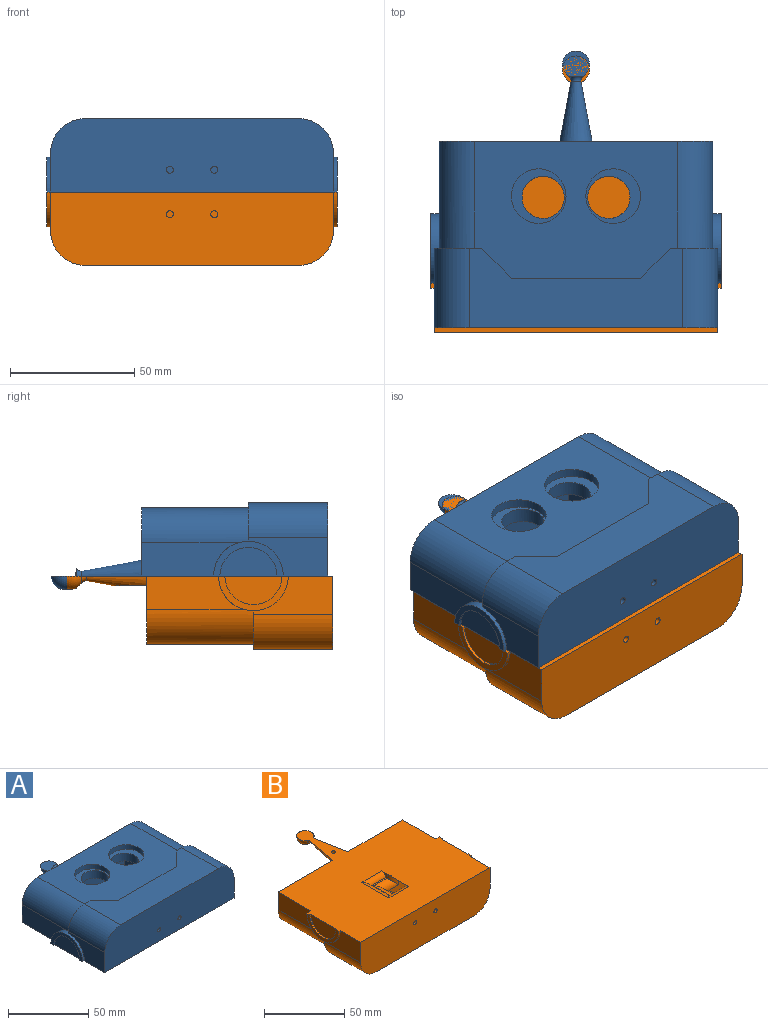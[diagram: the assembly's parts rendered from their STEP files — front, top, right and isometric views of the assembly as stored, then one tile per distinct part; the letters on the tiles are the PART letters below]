
ASSEMBLY  parts=2 mates=1
PART A: 52 faces, bbox 117x111.5x35 mm
  f0: cylinder r=8.5mm len=17mm, axis (0,0,1), area 320.4mm2, adj f1,f51
  f1: plane 22x22mm, normal (0,0,1), area 153.2mm2, adj f0,f2
  f2: cylinder r=11mm len=22mm, axis (0,0,1), area 241.9mm2, adj f1,f3
  f3: plane 82x55.04mm, normal (0,0,1), area 3536.4mm2, adj f2,f4,f41,f42,f43,f44,f45,f46
  f4: plane 12.04x12mm, normal (-0.71,0.71,0), area 34mm2, adj f3,f5,f41,f47
  f5: plane 86x32mm, normal (0,0,1), area 1981.3mm2, adj f4,f6,f35,f40,f41,f42,f43,f47
  f6: cylinder r=14mm len=32mm, axis (0,-1,0), area 703.7mm2, adj f5,f7,f35,f47
  f7: plane 32x15.5mm, normal (1,0,0), area 342.1mm2, adj f6,f8,f13,f35,f47
  f8: cylinder r=14mm len=28mm, axis (-1,0,0), area 109.9mm2, adj f7,f9,f10,f13,f46,f47
  f9: plane 39.31x13.52mm, normal (1,0,0), area 427.8mm2, adj f8,f13,f45,f46
  f10: plane 28x14mm, normal (1,0,0), area 100.1mm2, adj f8,f11,f13
  f11: cylinder r=11.5mm len=23mm, axis (-1,0,0), area 36.1mm2, adj f10,f12,f13
  f12: plane 23x11.5mm, normal (1,0,0), area 207.7mm2, adj f11,f13
  f13: plane 117x111.46mm, normal (0,0,-1), area 7484.9mm2, adj f7,f8,f9,f10,f11,f12,f14,f15
  f14: sphere r=5.5mm, area 175.7mm2, adj f13,f15
  f15: torus R=3.97mm, axis (0,-1,0), area 16.9mm2, adj f13,f14,f16
  f16: cone r=2mm half-angle=10.5deg, axis (0,-1,0), area 329.1mm2, adj f13,f15,f45
  f17: plane 39.31x13.52mm, normal (-1,0,0), area 427.8mm2, adj f13,f21,f44,f45
  f18: plane 23x11.5mm, normal (-1,0,0), area 207.7mm2, adj f13,f19
  f19: cylinder r=11.5mm len=23mm, axis (1,0,0), area 36.1mm2, adj f13,f18,f20
  f20: plane 28x14mm, normal (-1,0,0), area 100.1mm2, adj f13,f19,f21
  f21: cylinder r=14mm len=28mm, axis (1,0,0), area 110.1mm2, adj f13,f17,f20,f22,f43,f44
  f22: plane 32x15.5mm, normal (-1,0,0), area 342.1mm2, adj f13,f21,f35,f40,f43
  f23: plane 22x18mm, normal (1,0,0), area 396mm2, adj f13,f24,f32,f51
  f24: plane 47x18mm, normal (0,-1,0), area 846mm2, adj f13,f23,f25,f51
  f25: plane 22x18mm, normal (-1,0,0), area 396mm2, adj f13,f24,f32,f51
  f26: cylinder r=5mm len=17mm, axis (0,0,1), area 133.5mm2, adj f13,f27,f28,f32
  f27: plane 23.5x18mm, normal (0,0,-1), area 253.7mm2, adj f26,f28,f29,f30,f31,f32
  f28: plane 17x13mm, normal (-1,0,0), area 221mm2, adj f13,f26,f27,f29
  f29: plane 17x13.5mm, normal (0,1,0), area 229.5mm2, adj f13,f27,f28,f30
  f30: plane 17x13mm, normal (1,0,0), area 221mm2, adj f13,f27,f29,f31
  f31: cylinder r=5mm len=17mm, axis (0,0,1), area 133.5mm2, adj f13,f27,f30,f32
  f32: plane 47x18mm, normal (0,1,0), area 446.5mm2, adj f13,f23,f25,f26,f27,f31,f51
  f33: cylinder r=1.4mm len=4mm, axis (0,0,-1), area 35.2mm2, adj f13,f34
  f34: plane 2.8x2.8mm, normal (0,0,-1), area 6.2mm2, adj f33
  f35: plane 114x29.5mm, normal (0,-1,0), area 3266.6mm2, adj f5,f6,f7,f13,f22,f36,f38,f40
  f36: cylinder r=1.4mm len=10mm, axis (0,-1,0), area 88mm2, adj f35,f37
  f37: plane 2.8x2.8mm, normal (0,-1,0), area 6.2mm2, adj f36
  f38: cylinder r=1.4mm len=10mm, axis (0,-1,0), area 88mm2, adj f35,f39
  f39: plane 2.8x2.8mm, normal (0,-1,0), area 6.2mm2, adj f38
  f40: cylinder r=14mm len=32mm, axis (0,-1,0), area 703.7mm2, adj f5,f22,f35,f43
  f41: plane 52x2mm, normal (0,1,0), area 104mm2, adj f3,f4,f5,f42
  f42: plane 12.04x12mm, normal (0.71,0.71,0), area 34mm2, adj f3,f5,f41,f43
  f43: plane 19.02x15.62mm, normal (0,1,0), area 65mm2, adj f3,f5,f21,f22,f40,f42,f44
  f44: cylinder r=14mm len=43mm, axis (0,1,0), area 944.7mm2, adj f3,f17,f21,f43,f45
  f45: plane 110x27.5mm, normal (0,1,0), area 2874.5mm2, adj f3,f9,f13,f16,f17,f44,f46
  f46: cylinder r=14mm len=43mm, axis (0,-1,0), area 944.7mm2, adj f3,f8,f9,f45,f47
  f47: plane 19.02x15.62mm, normal (0,1,0), area 65mm2, adj f3,f4,f5,f6,f7,f8,f46
  f48: cylinder r=11mm len=22mm, axis (0,0,1), area 241.9mm2, adj f3,f49
  f49: plane 22x22mm, normal (0,0,1), area 153.2mm2, adj f48,f50
  f50: cylinder r=8.5mm len=17mm, axis (0,0,1), area 320.4mm2, adj f49,f51
  f51: plane 47x22mm, normal (0,0,-1), area 580mm2, adj f0,f23,f24,f25,f32,f50
PART B: 66 faces, bbox 117.4x111.9x29.9 mm
  f0: plane 18.53x15.62mm, normal (0,1,0), area 63.9mm2, adj f1,f2,f11,f14,f15,f24,f50
  f1: plane 86x32mm, normal (0,0,-1), area 992.9mm2, adj f0,f3,f5,f6,f13,f14,f33,f34
  f2: plane 82x43mm, normal (0,0,-1), area 1071.7mm2, adj f0,f6,f10,f15,f16,f32,f34,f35
  f3: plane 16x16mm, normal (-1,0,0), area 256mm2, adj f1,f33,f38,f60
  f4: plane 16.13x13.5mm, normal (0,0,1), area 37.7mm2, adj f47,f56,f57,f63,f64,f65
  f5: plane 114x29.5mm, normal (0,-1,0), area 3266.6mm2, adj f1,f11,f12,f13,f14,f20,f22,f31
  f6: plane 26.02x15.62mm, normal (0,1,0), area 78.9mm2, adj f1,f2,f12,f13,f16,f28,f34
  f7: plane 39.31x13.52mm, normal (-1,0,0), area 427.8mm2, adj f10,f16,f28,f31
  f8: cylinder r=11.5mm len=23mm, axis (-1,0,0), area 36.1mm2, adj f25,f26,f31
  f9: plane 39.31x13.52mm, normal (1,0,0), area 427.8mm2, adj f10,f15,f24,f31
  f10: plane 110x27.5mm, normal (0,1,0), area 2892.4mm2, adj f2,f7,f9,f15,f16,f18,f31,f54
  f11: plane 32x15.5mm, normal (1,0,0), area 342.1mm2, adj f0,f5,f14,f24,f31
  f12: plane 32x15.5mm, normal (-1,0,0), area 342.1mm2, adj f5,f6,f13,f28,f31
  f13: cylinder r=14mm len=32mm, axis (0,-1,0), area 703.7mm2, adj f1,f5,f6,f12
  f14: cylinder r=14mm len=32mm, axis (0,-1,0), area 703.7mm2, adj f0,f1,f5,f11
  f15: cylinder r=14mm len=43mm, axis (0,1,0), area 944.7mm2, adj f0,f2,f9,f10,f24
  f16: cylinder r=14mm len=43mm, axis (0,-1,0), area 944.7mm2, adj f2,f6,f7,f10,f28
  f17: torus R=3.97mm, axis (0,-1,0), area 16.9mm2, adj f18,f19,f31
  f18: cone r=2mm half-angle=10.5deg, axis (0,-1,0), area 231.2mm2, adj f10,f17,f31,f54
  f19: sphere r=5.5mm, area 175.7mm2, adj f17,f31
  f20: cylinder r=1.4mm len=10mm, axis (0,-1,0), area 88mm2, adj f5,f21
  f21: plane 2.8x2.8mm, normal (0,-1,0), area 6.2mm2, adj f20
  f22: cylinder r=1.4mm len=10mm, axis (0,-1,0), area 88mm2, adj f5,f23
  f23: plane 2.8x2.8mm, normal (0,-1,0), area 6.2mm2, adj f22
  f24: cylinder r=14mm len=28mm, axis (-1,0,0), area 110.1mm2, adj f0,f9,f11,f15,f25,f31
  f25: plane 28x14mm, normal (1,0,0), area 100.1mm2, adj f8,f24,f31
  f26: plane 23x11.5mm, normal (1,0,0), area 207.7mm2, adj f8,f31
  f27: cylinder r=11.5mm len=23mm, axis (1,0,0), area 36.1mm2, adj f29,f30,f31
  f28: cylinder r=14mm len=28mm, axis (1,0,0), area 109.9mm2, adj f6,f7,f12,f16,f29,f31
  f29: plane 28x14mm, normal (-1,0,0), area 100.1mm2, adj f27,f28,f31
  f30: plane 23x11.5mm, normal (-1,0,0), area 207.7mm2, adj f27,f31
  f31: plane 117x111.46mm, normal (0,0,1), area 8357.9mm2, adj f5,f7,f8,f9,f10,f11,f12,f17
  f32: plane 14x5mm, normal (-1,0,0), area 70mm2, adj f2,f38,f59,f62
  f33: plane 62x16mm, normal (0,1,0), area 992mm2, adj f1,f3,f34,f38
  f34: plane 66x16mm, normal (1,0,0), area 979mm2, adj f1,f2,f6,f33,f35,f38
  f35: plane 62x14mm, normal (0,-1,0), area 868mm2, adj f2,f34,f36,f38
  f36: plane 14x10mm, normal (-1,0,0), area 140mm2, adj f2,f35,f38,f61
  f37: plane 14x5mm, normal (-1,0,0), area 70mm2, adj f2,f38,f61,f62
  f38: plane 67x66mm, normal (0,0,-1), area 3892.2mm2, adj f3,f32,f33,f34,f35,f36,f37,f39
  f39: cylinder r=1.4mm len=7mm, axis (0,0,-1), area 61.6mm2, adj f38,f40
  f40: plane 2.8x2.8mm, normal (0,0,-1), area 6.2mm2, adj f39
  f41: cylinder r=1.4mm len=7mm, axis (0,0,-1), area 61.6mm2, adj f38,f42
  f42: plane 2.8x2.8mm, normal (0,0,-1), area 6.2mm2, adj f41
  f43: cylinder r=1.4mm len=7mm, axis (0,0,-1), area 61.6mm2, adj f38,f44
  f44: plane 2.8x2.8mm, normal (0,0,-1), area 6.2mm2, adj f43
  f45: cylinder r=1.4mm len=7mm, axis (0,0,-1), area 61.6mm2, adj f38,f46
  f46: plane 2.8x2.8mm, normal (0,0,-1), area 6.2mm2, adj f45
  f47: plane 4.87x3mm, normal (-1,0,0), area 6mm2, adj f4,f31,f58,f63
  f48: plane 48.22x25.5mm, normal (0,1,0), area 506.7mm2, adj f1,f38,f50,f51,f53,f56,f60,f65
  f49: plane 43.59x26.44mm, normal (0,-1,0), area 517.9mm2, adj f2,f38,f51,f52,f53,f57,f58,f59
  f50: plane 6.5x2mm, normal (-1,0,0), area 13mm2, adj f0,f1,f48,f53
  f51: plane 12.17x11.15mm, normal (0.65,0,0.76), area 144.8mm2, adj f38,f48,f49,f56,f57
  f52: cylinder r=47.35mm len=21.78mm, axis (0,-1,0), area 286.8mm2, adj f31,f49,f53,f58,f65
  f53: cylinder r=14mm len=26.44mm, axis (0,-1,0), area 414.5mm2, adj f2,f48,f49,f50,f52,f65
  f54: plane 13.46x10.25mm, normal (0,0,-1), area 81.3mm2, adj f10,f18,f55
  f55: cylinder r=1.4mm len=4mm, axis (0,0,-1), area 35.2mm2, adj f31,f54
  f56: cylinder r=5mm len=15.13mm, axis (0,1,0), area 47.9mm2, adj f4,f48,f51,f57,f65
  f57: cylinder r=5mm len=16.9mm, axis (1,0,0), area 83.9mm2, adj f4,f49,f51,f56,f58
  f58: cylinder r=5mm len=8mm, axis (0,0,1), area 38.2mm2, adj f47,f49,f52,f57
  f59: cylinder r=5mm len=14mm, axis (0,0,1), area 110mm2, adj f2,f32,f38,f49
  f60: cylinder r=5mm len=16mm, axis (0,0,1), area 125.7mm2, adj f1,f3,f38,f48
  f61: cylinder r=5mm len=14mm, axis (0,0,-1), area 110mm2, adj f2,f36,f37,f38
  f62: cylinder r=5mm len=14mm, axis (0,0,-1), area 110mm2, adj f2,f32,f37,f38
  f63: cylinder r=4mm len=17.37mm, axis (1,0,0), area 81.4mm2, adj f4,f31,f47,f64
  f64: cylinder r=4mm len=23.87mm, axis (0,1,0), area 105.4mm2, adj f4,f31,f63,f65
  f65: cylinder r=4mm len=51.28mm, axis (1,0,0), area 179mm2, adj f4,f31,f48,f52,f53,f56,f64
PLACE A t=(-12.5,255.07,8.64)mm
PLACE B t=(-12.5,253.07,8.64)mm
MATE planar A.f13 <-> B.f31  axis (0,0,-1) through (45.25,235.57,36.14)mm
